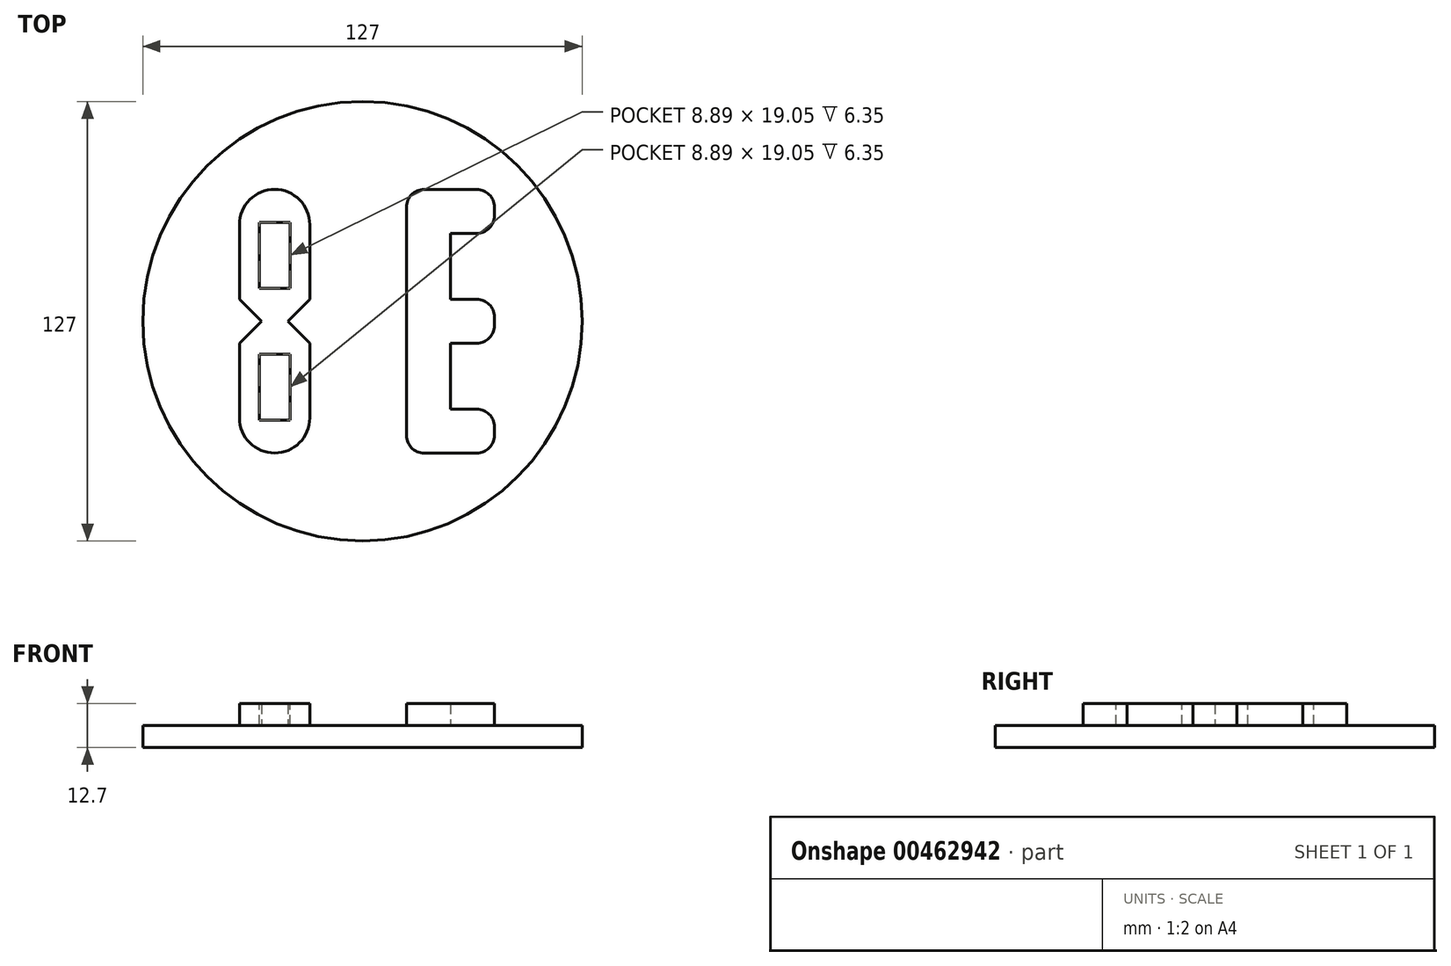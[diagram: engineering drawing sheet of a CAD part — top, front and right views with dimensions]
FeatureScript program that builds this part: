
annotation { "Feature Type Name" : "Feature", "Feature Type Description" : "" }
export const myFeature = defineFeature(function(context is Context, id is Id, definition is map)
    precondition{}
    {
        {
            var Q0;
            Q0=qCreatedBy(makeId("Top.planeOp"),FACE);
            var sketch = newSketch(context, id + "F0", { "sketchPlane" : qUnion([Q0])});
            skCircle(sketch, "E0", {"center": v(0, 0) * mm, "radius": 63.5 * mm});
            skSolve(sketch);
        }
        {
            var Q0;
            Q0 = qSketchRegion(id + "F0", true);
            extrude(context, id + "F1", {"entities" : qUnion([Q0]), "depth" : 6.35 * mm});
        }
        {
            var Q0;
            Q0=makeQuery(id+"F1.opExtrude","CAP_FACE",FACE,{"disambiguationData":[OSD([sQuery(id+"F0.wireOp",EDGE,"E0")])],"isStart":false});
            var sketch = newSketch(context, id + "F2", { "sketchPlane" : qUnion([Q0])});
            skLineSegment(sketch, "E1", {"start": v(-25.4, 0) * mm, "end": v(-29.21, 0) * mm});
            skLineSegment(sketch, "E2", {"start": v(-25.4, 0) * mm, "end": v(-21.59, 0) * mm});
            skLineSegment(sketch, "E3", {"start": v(-25.4, 0) * mm, "end": v(0, 0) * mm});
            skLineSegment(sketch, "E4", {"start": v(-35.56, 6.35) * mm, "end": v(-29.2, 0) * mm});
            skLineSegment(sketch, "E5", {"start": v(-21.59, 0) * mm, "end": v(-15.24, 6.35) * mm});
            skLineSegment(sketch, "E6", {"start": v(-21.59, 0) * mm, "end": v(-15.24, -6.35) * mm});
            skLineSegment(sketch, "E7", {"start": v(-29.21, 0) * mm, "end": v(-35.56, -6.35) * mm});
            skLineSegment(sketch, "E8", {"start": v(-35.56, -6.35) * mm, "end": v(-35.56, -38.1) * mm});
            skLineSegment(sketch, "E9", {"start": v(-15.24, -6.35) * mm, "end": v(-15.24, -38.1) * mm});
            skLineSegment(sketch, "E10", {"start": v(-15.24, -38.1) * mm, "end": v(-35.56, -38.1) * mm});
            skLineSegment(sketch, "E11", {"start": v(-35.56, 6.35) * mm, "end": v(-35.56, 38.1) * mm});
            skLineSegment(sketch, "E12", {"start": v(-15.24, 6.35) * mm, "end": v(-15.24, 38.1) * mm});
            skLineSegment(sketch, "E13", {"start": v(-35.56, 38.1) * mm, "end": v(-15.24, 38.1) * mm});
            skSolve(sketch);
        }
        {
            var Q0;
            Q0 = qSketchRegion(id + "F2", true);
            extrude(context, id + "F3", {"entities" : qUnion([Q0]), "operationType" : NewBodyOperationType.ADD, "depth" : 6.35 * mm});
        }
        {
            var Q0;
            Q0=makeQuery(id+"F1.opExtrude","CAP_FACE",FACE,{"disambiguationData":[OSD([sQuery(id+"F0.wireOp",EDGE,"E0")])],"isStart":false});
            var sketch = newSketch(context, id + "F4", { "sketchPlane" : qUnion([Q0])});
            skLineSegment(sketch, "E14", {"start": v(0, 0) * mm, "end": v(12.7, 0) * mm});
            skLineSegment(sketch, "E15", {"start": v(12.7, 0) * mm, "end": v(12.7, 38.1) * mm});
            skLineSegment(sketch, "E16", {"start": v(12.7, 0) * mm, "end": v(12.7, -38.1) * mm});
            skLineSegment(sketch, "E17", {"start": v(12.7, 38.1) * mm, "end": v(25.4, 38.1) * mm});
            skLineSegment(sketch, "E18", {"start": v(12.7, -38.1) * mm, "end": v(25.4, -38.1) * mm});
            skLineSegment(sketch, "E19", {"start": v(25.4, 38.1) * mm, "end": v(38.1, 38.1) * mm});
            skLineSegment(sketch, "E20", {"start": v(38.1, 38.1) * mm, "end": v(38.1, 25.4) * mm});
            skLineSegment(sketch, "E21", {"start": v(38.1, 25.4) * mm, "end": v(25.4, 25.4) * mm});
            skLineSegment(sketch, "E22", {"start": v(25.4, -38.1) * mm, "end": v(38.1, -38.1) * mm});
            skLineSegment(sketch, "E23", {"start": v(38.1, -38.1) * mm, "end": v(38.1, -25.4) * mm});
            skLineSegment(sketch, "E24", {"start": v(38.1, -25.4) * mm, "end": v(25.4, -25.4) * mm});
            skLineSegment(sketch, "E25", {"start": v(25.4, 0) * mm, "end": v(25.4, -6.35) * mm});
            skLineSegment(sketch, "E26", {"start": v(25.4, 0) * mm, "end": v(25.4, 6.35) * mm});
            skLineSegment(sketch, "E27", {"start": v(25.4, 38.1) * mm, "end": v(25.4, -38.1) * mm});
            skLineSegment(sketch, "E28", {"start": v(25.4, 6.35) * mm, "end": v(38.1, 6.35) * mm});
            skLineSegment(sketch, "E29", {"start": v(25.4, -6.35) * mm, "end": v(38.1, -6.35) * mm});
            skLineSegment(sketch, "E30", {"start": v(38.1, 6.35) * mm, "end": v(38.1, -6.35) * mm});
            skSolve(sketch);
        }
        {
            var Q0;
            Q0 = qSketchRegion(id + "F4", true);
            extrude(context, id + "F5", {"entities" : qUnion([Q0]), "operationType" : NewBodyOperationType.ADD, "depth" : 6.35 * mm});
        }
        {
            var Q0;
            Q0=makeQuery(id+"F3.opExtrude","SWEPT_EDGE",EDGE,{"disambiguationData":[OSD([sQuery(id+"F2.wireOp",EDGE,"E8"),sQuery(id+"F2.wireOp",EDGE,"E10")])]});
            var Q1;
            Q1=makeQuery(id+"F3.opExtrude","SWEPT_EDGE",EDGE,{"disambiguationData":[OSD([sQuery(id+"F2.wireOp",EDGE,"E9"),sQuery(id+"F2.wireOp",EDGE,"E10")])]});
            var Q2;
            Q2=makeQuery(id+"F3.opExtrude","SWEPT_EDGE",EDGE,{"disambiguationData":[OSD([sQuery(id+"F2.wireOp",EDGE,"E12"),sQuery(id+"F2.wireOp",EDGE,"E13")])]});
            var Q3;
            Q3=makeQuery(id+"F3.opExtrude","SWEPT_EDGE",EDGE,{"disambiguationData":[OSD([sQuery(id+"F2.wireOp",EDGE,"E11"),sQuery(id+"F2.wireOp",EDGE,"E13")])]});
            fillet(context, id + "F6", {"entities" : qUnion([Q0, Q1, Q2, Q3]), "radius" : 10.16 * mm, "tangentPropagation" : true, "allowEdgeOverflow" : false});
        }
        {
            var Q0;
            Q0=makeQuery(id+"F3.opExtrude","SWEPT_EDGE",EDGE,{"disambiguationData":[OSD([sQuery(id+"F2.wireOp",EDGE,"32zXh6H7-rDBc-Ws2k-Tw8j-ssj2XlCoOyZG"),sQuery(id+"F2.wireOp",EDGE,"8l8F8GZu-EmPQ-4rrn-lq95-TnQLBTggqvwZ")])]});
            var Q1;
            Q1=makeQuery(id+"F3.opExtrude","SWEPT_EDGE",EDGE,{"disambiguationData":[OSD([sQuery(id+"F2.wireOp",EDGE,"OPyV587z-79rD-ThT2-f9bQ-5MwLdGssQgCO"),sQuery(id+"F2.wireOp",EDGE,"RtBCrTOg-JrtW-5pMz-pE2T-e8IgMe5ByC1o")])]});
            var Q2;
            Q2=makeQuery(id+"F3.opExtrude","SWEPT_EDGE",EDGE,{"disambiguationData":[OSD([sQuery(id+"F2.wireOp",EDGE,"LiRUXX0V-k6R1-6890-TdLy-HnUKQTqBNajF"),sQuery(id+"F2.wireOp",EDGE,"x9WD0ybc-7O2d-nmyu-R6ek-ebGA4LNhR1tT")])]});
            var Q3;
            Q3=makeQuery(id+"F3.opExtrude","SWEPT_EDGE",EDGE,{"disambiguationData":[OSD([sQuery(id+"F2.wireOp",EDGE,"pvHd15Xp-c0bm-mIWi-SrLD-1pJ1LuWtH4ty"),sQuery(id+"F2.wireOp",EDGE,"uyF9bEem-UW9F-UzFf-iPNx-QGD3t7fa7oEc")])]});
            var Q4;
            Q4=makeQuery(id+"F5.opExtrude","SWEPT_EDGE",EDGE,{"disambiguationData":[OSD([sQuery(id+"F4.wireOp",EDGE,"E28"),sQuery(id+"F4.wireOp",EDGE,"E30")])]});
            var Q5;
            Q5=makeQuery(id+"F5.opExtrude","SWEPT_EDGE",EDGE,{"disambiguationData":[OSD([sQuery(id+"F4.wireOp",EDGE,"E29"),sQuery(id+"F4.wireOp",EDGE,"E30")])]});
            var Q6;
            Q6=makeQuery(id+"F5.opExtrude","SWEPT_EDGE",EDGE,{"disambiguationData":[OSD([sQuery(id+"F4.wireOp",EDGE,"E22"),sQuery(id+"F4.wireOp",EDGE,"E23")])]});
            var Q7;
            Q7=makeQuery(id+"F5.opExtrude","SWEPT_EDGE",EDGE,{"disambiguationData":[OSD([sQuery(id+"F4.wireOp",EDGE,"E23"),sQuery(id+"F4.wireOp",EDGE,"E24")])]});
            var Q8;
            Q8=makeQuery(id+"F5.opExtrude","SWEPT_EDGE",EDGE,{"disambiguationData":[OSD([sQuery(id+"F4.wireOp",EDGE,"E20"),sQuery(id+"F4.wireOp",EDGE,"E21")])]});
            var Q9;
            Q9=makeQuery(id+"F5.opExtrude","SWEPT_EDGE",EDGE,{"disambiguationData":[OSD([sQuery(id+"F4.wireOp",EDGE,"E19"),sQuery(id+"F4.wireOp",EDGE,"E20")])]});
            var Q10;
            Q10=makeQuery(id+"F5.opExtrude","SWEPT_EDGE",EDGE,{"disambiguationData":[OSD([sQuery(id+"F4.wireOp",EDGE,"E15"),sQuery(id+"F4.wireOp",EDGE,"E17")])]});
            var Q11;
            Q11=makeQuery(id+"F5.opExtrude","SWEPT_EDGE",EDGE,{"disambiguationData":[OSD([sQuery(id+"F4.wireOp",EDGE,"E16"),sQuery(id+"F4.wireOp",EDGE,"E18")])]});
            fillet(context, id + "F7", {"entities" : qUnion([Q0, Q1, Q2, Q3, Q4, Q5, Q6, Q7, Q8, Q9, Q10, Q11]), "radius" : 5.08 * mm, "tangentPropagation" : true, "allowEdgeOverflow" : false});
        }
        {
            var Q0;
            Q0=makeQuery(id+"F3.opExtrude","CAP_FACE",FACE,{"disambiguationData":[OSD([sQuery(id+"F2.wireOp",EDGE,"E4"),sQuery(id+"F2.wireOp",EDGE,"E5"),sQuery(id+"F2.wireOp",EDGE,"E6"),sQuery(id+"F2.wireOp",EDGE,"E7"),sQuery(id+"F2.wireOp",EDGE,"E8"),sQuery(id+"F2.wireOp",EDGE,"E9"),sQuery(id+"F2.wireOp",EDGE,"E10"),sQuery(id+"F2.wireOp",EDGE,"E11"),sQuery(id+"F2.wireOp",EDGE,"E12"),sQuery(id+"F2.wireOp",EDGE,"E13")])],"isStart":false});
            var sketch = newSketch(context, id + "F8", { "sketchPlane" : qUnion([Q0])});
            skLineSegment(sketch, "E31", {"start": v(-29.21, 0) * mm, "end": v(-21.59, 0) * mm});
            skLineSegment(sketch, "E32", {"start": v(-21.59, 0) * mm, "end": v(-25.4, 0) * mm});
            skLineSegment(sketch, "E33", {"start": v(-25.4, 0) * mm, "end": v(-25.4, -19.05) * mm});
            skLineSegment(sketch, "E34.bottom", {"start": v(-20.95, -28.57) * mm, "end": v(-29.84, -28.57) * mm});
            skLineSegment(sketch, "E34.top", {"start": v(-20.95, -9.53) * mm, "end": v(-29.84, -9.53) * mm});
            skLineSegment(sketch, "E34.left", {"start": v(-20.95, -28.57) * mm, "end": v(-20.95, -9.53) * mm});
            skLineSegment(sketch, "E34.right", {"start": v(-29.84, -28.57) * mm, "end": v(-29.84, -9.53) * mm});
            skPoint(sketch, "E34.middle", {"position": v(-25.4, -19.05) * mm});
            skLineSegment(sketch, "E35.MirrorCS", {"start": v(-20.95, 9.53) * mm, "end": v(-29.84, 9.53) * mm});
            skLineSegment(sketch, "E36.MirrorCS", {"start": v(-29.84, 28.57) * mm, "end": v(-29.84, 9.53) * mm});
            skLineSegment(sketch, "E37.MirrorCS", {"start": v(-20.95, 28.57) * mm, "end": v(-20.95, 9.53) * mm});
            skLineSegment(sketch, "E38.MirrorCS", {"start": v(-20.96, 28.57) * mm, "end": v(-29.85, 28.57) * mm});
            skSolve(sketch);
        }
        {
            var Q0;
            Q0 = qSketchRegion(id + "F8", true);
            extrude(context, id + "F9", {"entities" : qUnion([Q0]), "operationType" : NewBodyOperationType.REMOVE, "oppositeDirection" : true, "depth" : 6.35 * mm});
        }
    });
